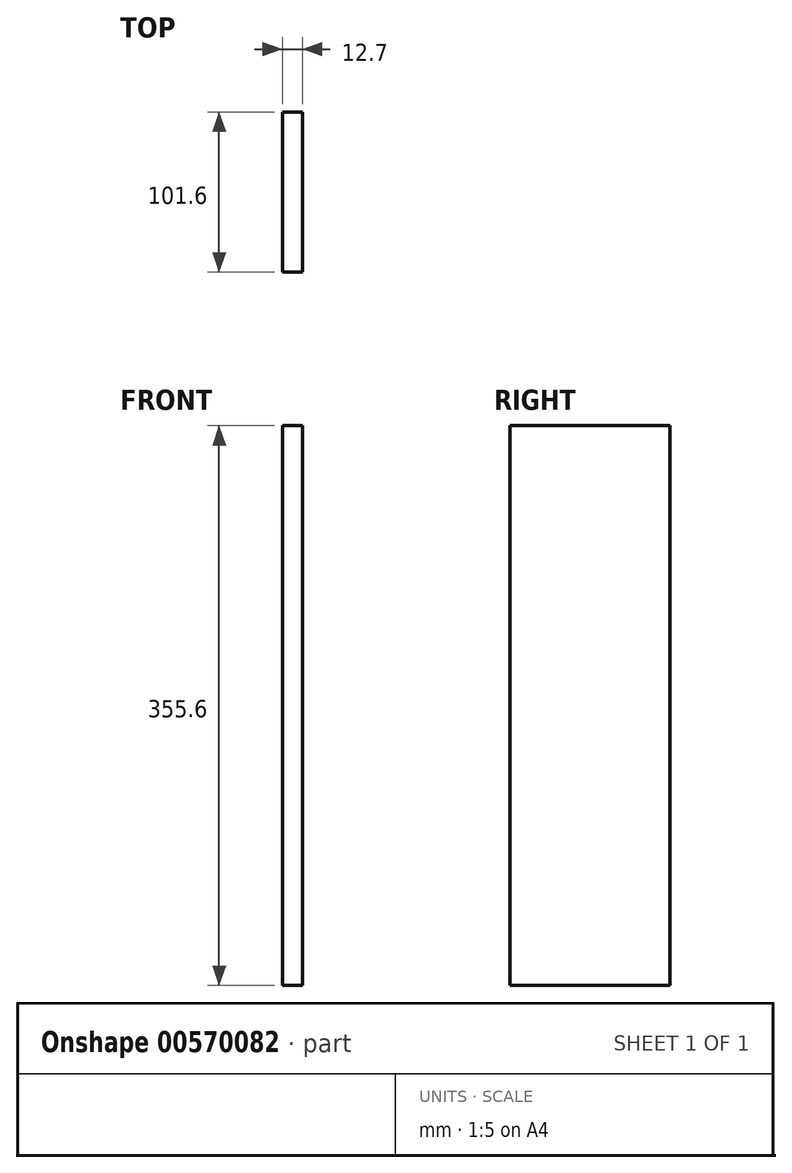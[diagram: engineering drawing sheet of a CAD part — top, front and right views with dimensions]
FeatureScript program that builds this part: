
annotation { "Feature Type Name" : "Feature", "Feature Type Description" : "" }
export const myFeature = defineFeature(function(context is Context, id is Id, definition is map)
    precondition{}
    {
        {
            var Q0;
            Q0=qCreatedBy(makeId("Right.planeOp"),FACE);
            var sketch = newSketch(context, id + "F0", { "sketchPlane" : qUnion([Q0])});
            skLineSegment(sketch, "E0", {"start": v(0, 0) * mm, "end": v(101.6, 0) * mm});
            skLineSegment(sketch, "E1", {"start": v(0, 0) * mm, "end": v(0, 355.6) * mm});
            skLineSegment(sketch, "E2", {"start": v(0, 355.6) * mm, "end": v(101.6, 355.6) * mm});
            skLineSegment(sketch, "E3", {"start": v(101.6, 355.6) * mm, "end": v(101.6, 0) * mm});
            skSolve(sketch);
        }
        {
            var Q0;
            Q0 = qSketchRegion(id + "F0", true);
            extrude(context, id + "F1", {"entities" : qUnion([Q0]), "oppositeDirection" : true, "depth" : 12.7 * mm, "offsetDistance" : 25.4 * mm});
        }
    });
